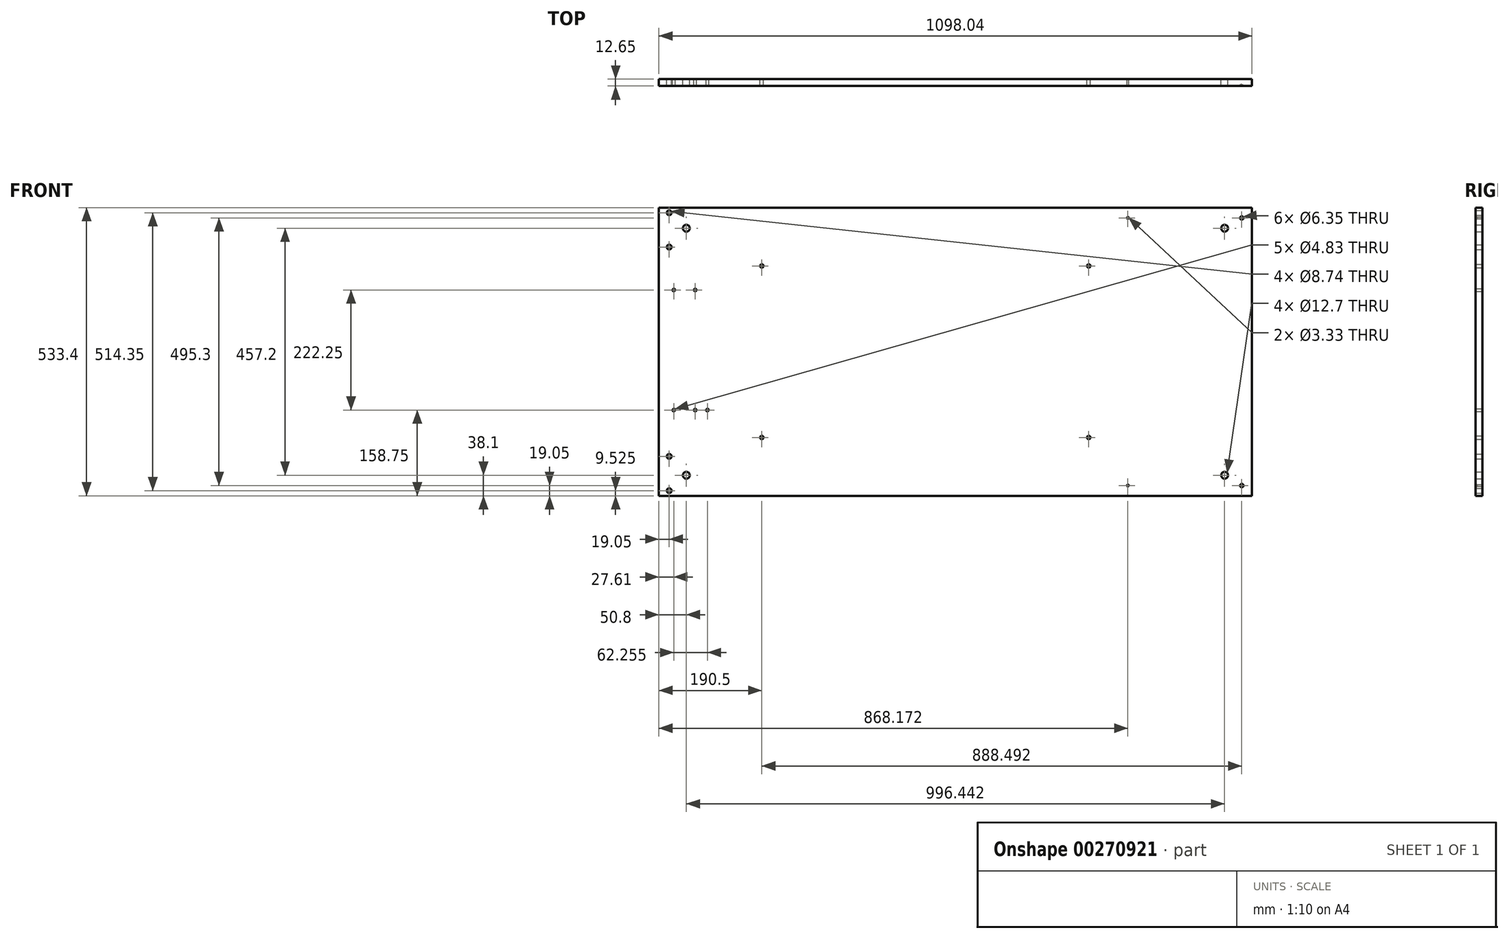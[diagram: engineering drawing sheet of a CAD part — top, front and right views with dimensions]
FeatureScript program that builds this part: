
annotation { "Feature Type Name" : "Feature", "Feature Type Description" : "" }
export const myFeature = defineFeature(function(context is Context, id is Id, definition is map)
    precondition{}
    {
        {
            var Q0;
            Q0=qCreatedBy(makeId("Front.planeOp"),FACE);
            var sketch = newSketch(context, id + "F0", { "sketchPlane" : qUnion([Q0])});
            skLineSegment(sketch, "E0.bottom", {"start": v(0, 0) * mm, "end": v(1098.04, 0) * mm});
            skLineSegment(sketch, "E0.top", {"start": v(0, 533.4) * mm, "end": v(1098.04, 533.4) * mm});
            skLineSegment(sketch, "E0.left", {"start": v(0, 0) * mm, "end": v(0, 533.4) * mm});
            skLineSegment(sketch, "E0.right", {"start": v(1098.04, 0) * mm, "end": v(1098.04, 533.4) * mm});
            skSolve(sketch);
        }
        {
            var Q0;
            Q0=makeQuery(id+"F0.imprint","IMPRINT",FACE,{"disambiguationData":[TD([[makeQuery(id+"F0.imprint","IMPRINT",EDGE,{"derivedFrom":sQuery(id+"F0.wireOp",EDGE,"E0.bottom")}),1.0]])]});
            extrude(context, id + "F1", {"entities" : qUnion([Q0]), "depth" : 12.65 * mm});
        }
        {
            var Q0;
            Q0=makeQuery(id+"F1.opExtrude","CAP_FACE",FACE,{"disambiguationData":[OSD([sQuery(id+"F0.wireOp",EDGE,"E0.bottom"),sQuery(id+"F0.wireOp",EDGE,"E0.top"),sQuery(id+"F0.wireOp",EDGE,"E0.left"),sQuery(id+"F0.wireOp",EDGE,"E0.right")])],"isStart":false});
            var sketch = newSketch(context, id + "F2", { "sketchPlane" : qUnion([Q0])});
            skLineSegment(sketch, "E1.bottom", {"start": v(1098.04, 533.4) * mm, "end": v(1059.94, 533.4) * mm});
            skLineSegment(sketch, "E1.top", {"start": v(1098.04, 495.3) * mm, "end": v(1059.94, 495.3) * mm});
            skLineSegment(sketch, "E1.left", {"start": v(1098.04, 533.4) * mm, "end": v(1098.04, 495.3) * mm});
            skLineSegment(sketch, "E1.right", {"start": v(1059.94, 533.4) * mm, "end": v(1059.94, 495.3) * mm});
            skLineSegment(sketch, "E2.bottom", {"start": v(1098.04, 0) * mm, "end": v(1059.94, 0) * mm});
            skLineSegment(sketch, "E2.top", {"start": v(1098.04, 38.1) * mm, "end": v(1059.94, 38.1) * mm});
            skLineSegment(sketch, "E2.left", {"start": v(1098.04, 0) * mm, "end": v(1098.04, 38.1) * mm});
            skLineSegment(sketch, "E2.right", {"start": v(1059.94, 0) * mm, "end": v(1059.94, 38.1) * mm});
            skLineSegment(sketch, "E3", {"start": v(1079, 38.1) * mm, "end": v(1079, 19.05) * mm});
            skPoint(sketch, "E3.endSnap0", {"position": v(1059.94, 19.05) * mm});
            skLineSegment(sketch, "E4", {"start": v(1079, 495.3) * mm, "end": v(1079, 514.35) * mm});
            skPoint(sketch, "E4.endSnap0", {"position": v(1059.94, 514.35) * mm});
            skSolve(sketch);
        }
        {
            var Q0;
            Q0=sQuery(id+"F2.wireOp",VERTEX,"E4.end");
            var Q1;
            Q1=sQuery(id+"F2.wireOp",VERTEX,"E3.end");
            var Q2;
            Q2=makeQuery(id+"F1.opExtrude","SWEPT_BODY",BODY,{"disambiguationData":[OSD([sQuery(id+"F0.wireOp",EDGE,"E0.bottom"),sQuery(id+"F0.wireOp",EDGE,"E0.top"),sQuery(id+"F0.wireOp",EDGE,"E0.left"),sQuery(id+"F0.wireOp",EDGE,"E0.right")])]});
            hole(context, id + "F3", {"style" : HoleStyle.SIMPLE, "endStyle" : HoleEndStyle.BLIND, "holeDiameter" : 6.35 * mm, "holeDepth" : 1.52 * mm, "tappedDepth" : 12.7 * mm, "tapClearance" : 3, "locations" : qUnion([Q0, Q1]), "scope" : qUnion([Q2])});
        }
        {
            var Q0;
            Q0=makeQuery(id+"F1.opExtrude","CAP_FACE",FACE,{"disambiguationData":[OSD([sQuery(id+"F0.wireOp",EDGE,"E0.bottom"),sQuery(id+"F0.wireOp",EDGE,"E0.top"),sQuery(id+"F0.wireOp",EDGE,"E0.left"),sQuery(id+"F0.wireOp",EDGE,"E0.right")])],"isStart":true});
            var sketch = newSketch(context, id + "F4", { "sketchPlane" : qUnion([Q0])});
            skLineSegment(sketch, "E5", {"start": v(-1098.04, 0) * mm, "end": v(-1098.04, 19.05) * mm});
            skLineSegment(sketch, "E6", {"start": v(-1098.04, 19.05) * mm, "end": v(-868.17, 19.05) * mm});
            skCircle(sketch, "E7", {"center": v(-868.17, 19.05) * mm, "radius": 1.66 * mm});
            skLineSegment(sketch, "E8", {"start": v(-1098.04, 0) * mm, "end": v(-1098.04, 107.95) * mm});
            skLineSegment(sketch, "E9", {"start": v(-1098.04, 107.95) * mm, "end": v(-795.65, 107.95) * mm});
            skCircle(sketch, "E10", {"center": v(-795.65, 107.95) * mm, "radius": 3.17 * mm});
            skLineSegment(sketch, "E11", {"start": v(-1098.04, 0) * mm, "end": v(-1098.04, 266.7) * mm});
            skLineSegment(sketch, "E12", {"start": v(-1098.04, 266.7) * mm, "end": v(-699.76, 266.7) * mm});
            skLineSegment(sketch, "E13.MirrorCS", {"start": v(-1098.04, 425.45) * mm, "end": v(-795.65, 425.45) * mm});
            skLineSegment(sketch, "E14.MirrorCS", {"start": v(-1098.04, 514.35) * mm, "end": v(-868.17, 514.35) * mm});
            skCircle(sketch, "E15.MirrorC", {"center": v(-795.65, 425.45) * mm, "radius": 3.17 * mm});
            skCircle(sketch, "E16.MirrorC", {"center": v(-868.17, 514.35) * mm, "radius": 1.66 * mm});
            skLineSegment(sketch, "E17", {"start": v(0, 0) * mm, "end": v(0, 14.15) * mm});
            skLineSegment(sketch, "E18", {"start": v(0, 0) * mm, "end": v(0, 68.4) * mm});
            skLineSegment(sketch, "E19", {"start": v(0, 0) * mm, "end": v(0, 107.95) * mm});
            skLineSegment(sketch, "E20", {"start": v(0, 107.95) * mm, "end": v(-190.5, 107.95) * mm});
            skCircle(sketch, "E21", {"center": v(-190.5, 107.95) * mm, "radius": 3.18 * mm});
            skLineSegment(sketch, "E22", {"start": v(0, 0) * mm, "end": v(0, 158.75) * mm});
            skLineSegment(sketch, "E23", {"start": v(0, 158.75) * mm, "end": v(-89.87, 158.75) * mm});
            skLineSegment(sketch, "E24", {"start": v(0, 158.75) * mm, "end": v(-27.6, 158.75) * mm});
            skLineSegment(sketch, "E25", {"start": v(-27.6, 158.75) * mm, "end": v(-67.23, 158.75) * mm});
            skCircle(sketch, "E26", {"center": v(-89.87, 158.75) * mm, "radius": 2.41 * mm});
            skCircle(sketch, "E27", {"center": v(-67.23, 158.75) * mm, "radius": 2.41 * mm});
            skCircle(sketch, "E28", {"center": v(-27.6, 158.75) * mm, "radius": 2.41 * mm});
            skLineSegment(sketch, "E29", {"start": v(0, 533.4) * mm, "end": v(0, 266.7) * mm});
            skCircle(sketch, "E30.MirrorC", {"center": v(-190.5, 425.45) * mm, "radius": 3.18 * mm});
            skCircle(sketch, "E31.MirrorC", {"center": v(-19.05, 460.38) * mm, "radius": 4.37 * mm});
            skCircle(sketch, "E32.MirrorC", {"center": v(-19.05, 523.88) * mm, "radius": 4.37 * mm});
            skLineSegment(sketch, "E33", {"start": v(-27.6, 374.65) * mm, "end": v(-27.6, 381) * mm});
            skLineSegment(sketch, "E34", {"start": v(-67.23, 374.65) * mm, "end": v(-67.23, 381) * mm});
            skCircle(sketch, "E35", {"center": v(-67.23, 381) * mm, "radius": 2.41 * mm});
            skCircle(sketch, "E36", {"center": v(-27.6, 381) * mm, "radius": 2.41 * mm});
            skLineSegment(sketch, "E37", {"start": v(0, 533.4) * mm, "end": v(-19.05, 533.4) * mm});
            skLineSegment(sketch, "E38", {"start": v(-19.05, 533.4) * mm, "end": v(-19.05, 523.88) * mm});
            skLineSegment(sketch, "E39", {"start": v(0, 0) * mm, "end": v(-19.05, 0) * mm});
            skLineSegment(sketch, "E40", {"start": v(-19.05, 0) * mm, "end": v(-19.05, 9.52) * mm});
            skCircle(sketch, "E41", {"center": v(-19.05, 9.52) * mm, "radius": 4.37 * mm});
            skCircle(sketch, "E42", {"center": v(-19.05, 73.03) * mm, "radius": 4.37 * mm});
            skLineSegment(sketch, "E43", {"start": v(0, 0) * mm, "end": v(0, 34.2) * mm});
            skLineSegment(sketch, "E44", {"start": v(0, 0) * mm, "end": v(0, 38.1) * mm});
            skLineSegment(sketch, "E45", {"start": v(0, 38.1) * mm, "end": v(-50.8, 38.1) * mm});
            skCircle(sketch, "E46", {"center": v(-50.8, 38.1) * mm, "radius": 6.35 * mm});
            skLineSegment(sketch, "E47", {"start": v(0, 533.4) * mm, "end": v(0, 495.3) * mm});
            skLineSegment(sketch, "E48", {"start": v(0, 495.3) * mm, "end": v(-50.8, 495.3) * mm});
            skCircle(sketch, "E49", {"center": v(-50.8, 495.3) * mm, "radius": 6.35 * mm});
            skLineSegment(sketch, "E50", {"start": v(-1098.04, 533.4) * mm, "end": v(-1098.04, 495.3) * mm});
            skLineSegment(sketch, "E51", {"start": v(-1098.04, 495.3) * mm, "end": v(-1047.24, 495.3) * mm});
            skCircle(sketch, "E52", {"center": v(-1047.24, 495.3) * mm, "radius": 6.35 * mm});
            skLineSegment(sketch, "E53", {"start": v(-1098.04, 0) * mm, "end": v(-1098.04, 38.1) * mm});
            skLineSegment(sketch, "E54", {"start": v(-1098.04, 38.1) * mm, "end": v(-1047.24, 38.1) * mm});
            skCircle(sketch, "E55", {"center": v(-1047.24, 38.1) * mm, "radius": 6.35 * mm});
            skSolve(sketch);
        }
        {
            var Q0;
            Q0 = qSketchRegion(id + "F4", true);
            extrude(context, id + "F5", {"entities" : qUnion([Q0]), "operationType" : NewBodyOperationType.REMOVE, "oppositeDirection" : true, "depth" : 25.4 * mm});
        }
    });
